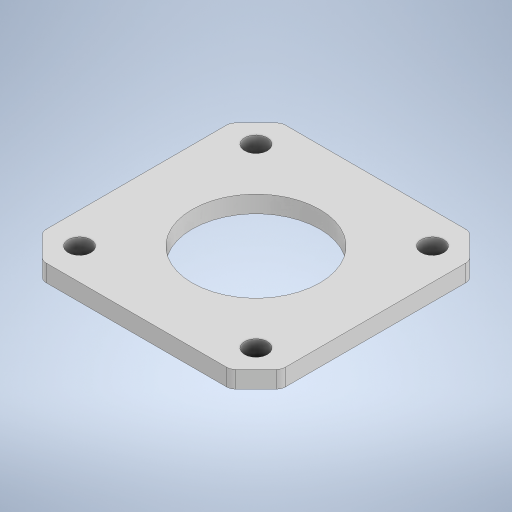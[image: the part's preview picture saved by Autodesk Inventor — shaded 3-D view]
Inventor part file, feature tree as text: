
AUTODESK INVENTOR PART (.ipt)
format: ipt  version: 2024 (Build 280153000, 153)  size: 419,328 bytes
history: native  units: mm
features: other x3, plane x1, extrude x1, sketch x1, reference x1
ambient origin geometry x8: Origin, YZ Plane, XZ Plane, XY Plane, X Axis, Y Axis, Z Axis, Center Point
bodies: Solid1 (feature_tree)
feature tree (7):
  plane  "Work Plane1"
  extrude  "Extrusion1"  Depth=3.0mm
  sketch  "Sketch1"  dims[d0=4.0mm d1=4.0mm d2=4.0mm d3=4.0mm d4=3.0mm d5=0.0mm]
  reference  "Reference1"
  other  "<userpath> windows\Documents\Inventor\Robotska_roka\roka.iam"
  other  "roka.iam"
  other  "Nema 17 Motor a Pasos 17HS4401:3"
